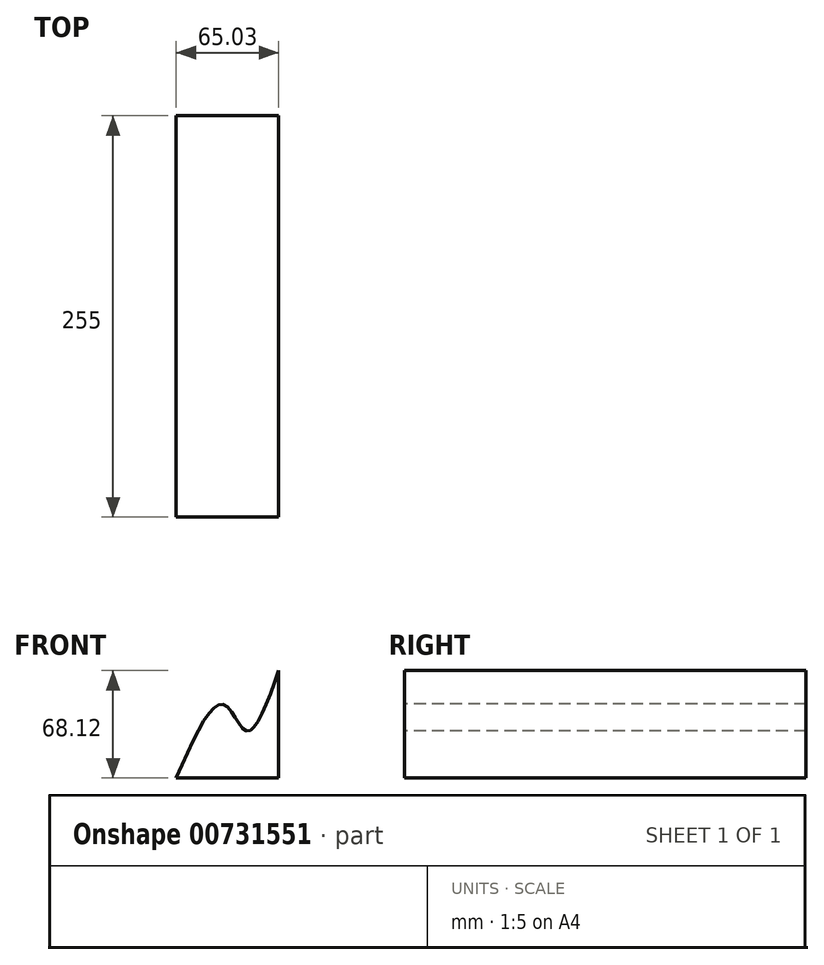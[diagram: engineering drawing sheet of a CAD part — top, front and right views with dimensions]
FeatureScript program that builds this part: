
annotation { "Feature Type Name" : "Feature", "Feature Type Description" : "" }
export const myFeature = defineFeature(function(context is Context, id is Id, definition is map)
    precondition{}
    {
        {
            var Q0;
            Q0=qCreatedBy(makeId("Front.planeOp"),FACE);
            var sketch = newSketch(context, id + "F0", { "sketchPlane" : qUnion([Q0])});
            skLineSegment(sketch, "E0.bottom", {"start": v(0, 0) * mm, "end": v(65.03, 0) * mm});
            skLineSegment(sketch, "E0.top", {"start": v(0, 68.12) * mm, "end": v(65.03, 68.12) * mm});
            skLineSegment(sketch, "E0.left", {"start": v(0, 0) * mm, "end": v(0, 68.12) * mm});
            skLineSegment(sketch, "E0.right", {"start": v(65.03, 0) * mm, "end": v(65.03, 68.12) * mm});
            skFitSpline(sketch, "E1", {"points": [v(0, 0) * mm, v(30.27, 46.55) * mm, v(44.45, 29.97) * mm, v(65.03, 68.12) * mm], "startDerivative": vector(82.23, 187.14) * mm, "endDerivative": vector(60.1, 172.43) * mm});
            skSolve(sketch);
        }
        {
            var Q0;
            Q0=makeQuery(id+"F0.imprint","IMPRINT",FACE,{"disambiguationData":[TD([[makeQuery(id+"F0.imprint","IMPRINT",EDGE,{"derivedFrom":sQuery(id+"F0.wireOp",EDGE,"E0.bottom")}),1.0]])]});
            extrude(context, id + "F1", {"entities" : qUnion([Q0]), "depth" : 255 * mm, "offsetDistance" : 25.4 * mm});
        }
    });
